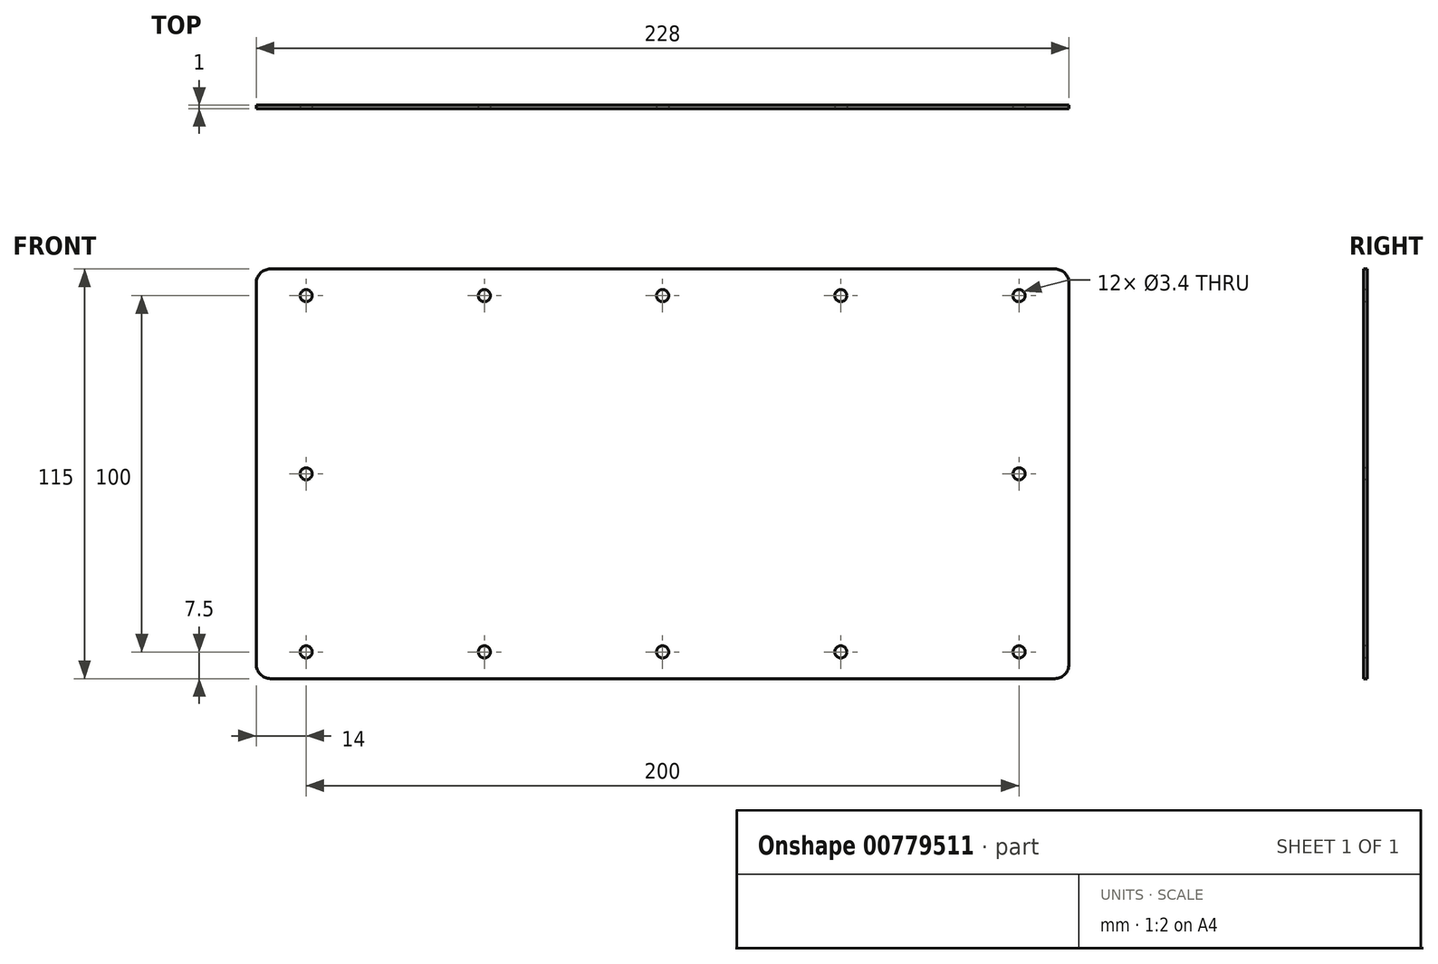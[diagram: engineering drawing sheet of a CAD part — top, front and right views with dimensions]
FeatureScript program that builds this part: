
annotation { "Feature Type Name" : "Feature", "Feature Type Description" : "" }
export const myFeature = defineFeature(function(context is Context, id is Id, definition is map)
    precondition{}
    {
        {
            var Q0;
            Q0=qCreatedBy(makeId("Front.planeOp"),FACE);
            var sketch = newSketch(context, id + "F0", { "sketchPlane" : qUnion([Q0])});
            skLineSegment(sketch, "E0.bottom", {"start": v(-114, 57.5) * mm, "end": v(114, 57.5) * mm});
            skLineSegment(sketch, "E0.top", {"start": v(-114, -57.5) * mm, "end": v(114, -57.5) * mm});
            skLineSegment(sketch, "E0.left", {"start": v(-114, 57.5) * mm, "end": v(-114, -57.5) * mm});
            skLineSegment(sketch, "E0.right", {"start": v(114, 57.5) * mm, "end": v(114, -57.5) * mm});
            skSolve(sketch);
        }
        {
            var Q0;
            Q0=makeQuery(id+"F0.imprint","IMPRINT",FACE,{"disambiguationData":[TD([[makeQuery(id+"F0.imprint","IMPRINT",EDGE,{"derivedFrom":sQuery(id+"F0.wireOp",EDGE,"E0.bottom")}),-1.0]])]});
            extrude(context, id + "F1", {"entities" : qUnion([Q0]), "depth" : 1 * mm, "offsetDistance" : 25 * mm});
        }
        {
            var Q0;
            Q0=makeQuery(id+"F1.opExtrude","SWEPT_EDGE",EDGE,{"disambiguationData":[OSD([sQuery(id+"F0.wireOp",EDGE,"E0.bottom"),sQuery(id+"F0.wireOp",EDGE,"E0.right")])]});
            var Q1;
            Q1=makeQuery(id+"F1.opExtrude","SWEPT_EDGE",EDGE,{"disambiguationData":[OSD([sQuery(id+"F0.wireOp",EDGE,"E0.bottom"),sQuery(id+"F0.wireOp",EDGE,"E0.left")])]});
            var Q2;
            Q2=makeQuery(id+"F1.opExtrude","SWEPT_EDGE",EDGE,{"disambiguationData":[OSD([sQuery(id+"F0.wireOp",EDGE,"E0.top"),sQuery(id+"F0.wireOp",EDGE,"E0.left")])]});
            var Q3;
            Q3=makeQuery(id+"F1.opExtrude","SWEPT_EDGE",EDGE,{"disambiguationData":[OSD([sQuery(id+"F0.wireOp",EDGE,"E0.top"),sQuery(id+"F0.wireOp",EDGE,"E0.right")])]});
            fillet(context, id + "F2", {"entities" : qUnion([Q0, Q1, Q2, Q3]), "radius" : 4 * mm, "tangentPropagation" : true, "allowEdgeOverflow" : false});
        }
        {
            var Q0;
            Q0=makeQuery(id+"F1.opExtrude","CAP_FACE",FACE,{"disambiguationData":[OSD([sQuery(id+"F0.wireOp",EDGE,"E0.bottom"),sQuery(id+"F0.wireOp",EDGE,"E0.top"),sQuery(id+"F0.wireOp",EDGE,"E0.left"),sQuery(id+"F0.wireOp",EDGE,"E0.right")])],"isStart":false});
            var sketch = newSketch(context, id + "F3", { "sketchPlane" : qUnion([Q0])});
            skLineSegment(sketch, "E1.bottom", {"start": v(-100, 50) * mm, "end": v(100, 50) * mm});
            skLineSegment(sketch, "E1.top", {"start": v(-100, -50) * mm, "end": v(100, -50) * mm});
            skLineSegment(sketch, "E1.left", {"start": v(-100, 50) * mm, "end": v(-100, -50) * mm});
            skLineSegment(sketch, "E1.right", {"start": v(100, 50) * mm, "end": v(100, -50) * mm});
            skLineSegment(sketch, "E2.bottom", {"start": v(-50, 50) * mm, "end": v(50, 50) * mm});
            skLineSegment(sketch, "E2.top", {"start": v(-50, -50) * mm, "end": v(50, -50) * mm});
            skLineSegment(sketch, "E2.left", {"start": v(-50, 50) * mm, "end": v(-50, -50) * mm});
            skLineSegment(sketch, "E2.right", {"start": v(50, 50) * mm, "end": v(50, -50) * mm});
            skLineSegment(sketch, "E3", {"start": v(0, 50) * mm, "end": v(0, -50) * mm});
            skLineSegment(sketch, "E4", {"start": v(-100, 0) * mm, "end": v(100, 0) * mm});
            skSolve(sketch);
        }
        {
            var Q0;
            Q0=sQuery(id+"F3.wireOp",VERTEX,"E2.bottom.start");
            var Q1;
            Q1=sQuery(id+"F3.wireOp",VERTEX,"E4.start");
            var Q2;
            Q2=sQuery(id+"F3.wireOp",VERTEX,"E1.left.end");
            var Q3;
            Q3=sQuery(id+"F3.wireOp",VERTEX,"E2.top.start");
            var Q4;
            Q4=sQuery(id+"F3.wireOp",VERTEX,"E1.bottom.start");
            var Q5;
            Q5=sQuery(id+"F3.wireOp",VERTEX,"E3.start");
            var Q6;
            Q6=sQuery(id+"F3.wireOp",VERTEX,"E1.right.end");
            var Q7;
            Q7=sQuery(id+"F3.wireOp",VERTEX,"E3.end");
            var Q8;
            Q8=sQuery(id+"F3.wireOp",VERTEX,"E2.top.end");
            var Q9;
            Q9=sQuery(id+"F3.wireOp",VERTEX,"E1.right.start");
            var Q10;
            Q10=sQuery(id+"F3.wireOp",VERTEX,"E4.end");
            var Q11;
            Q11=sQuery(id+"F3.wireOp",VERTEX,"E2.bottom.end");
            var Q12;
            Q12=makeQuery(id+"F1.opExtrude","SWEPT_BODY",BODY,{"disambiguationData":[OSD([sQuery(id+"F0.wireOp",EDGE,"E0.bottom"),sQuery(id+"F0.wireOp",EDGE,"E0.top"),sQuery(id+"F0.wireOp",EDGE,"E0.left"),sQuery(id+"F0.wireOp",EDGE,"E0.right")])]});
            hole(context, id + "F4", {"style" : HoleStyle.SIMPLE, "endStyle" : HoleEndStyle.THROUGH, "holeDiameter" : 3.4 * mm, "majorDiameter" : 5 * mm, "isTappedThrough" : true, "tappedDepth" : 12 * mm, "tapClearance" : 3, "locations" : qUnion([Q0, Q1, Q2, Q3, Q4, Q5, Q6, Q7, Q8, Q9, Q10, Q11]), "scope" : qUnion([Q12])});
        }
    });
